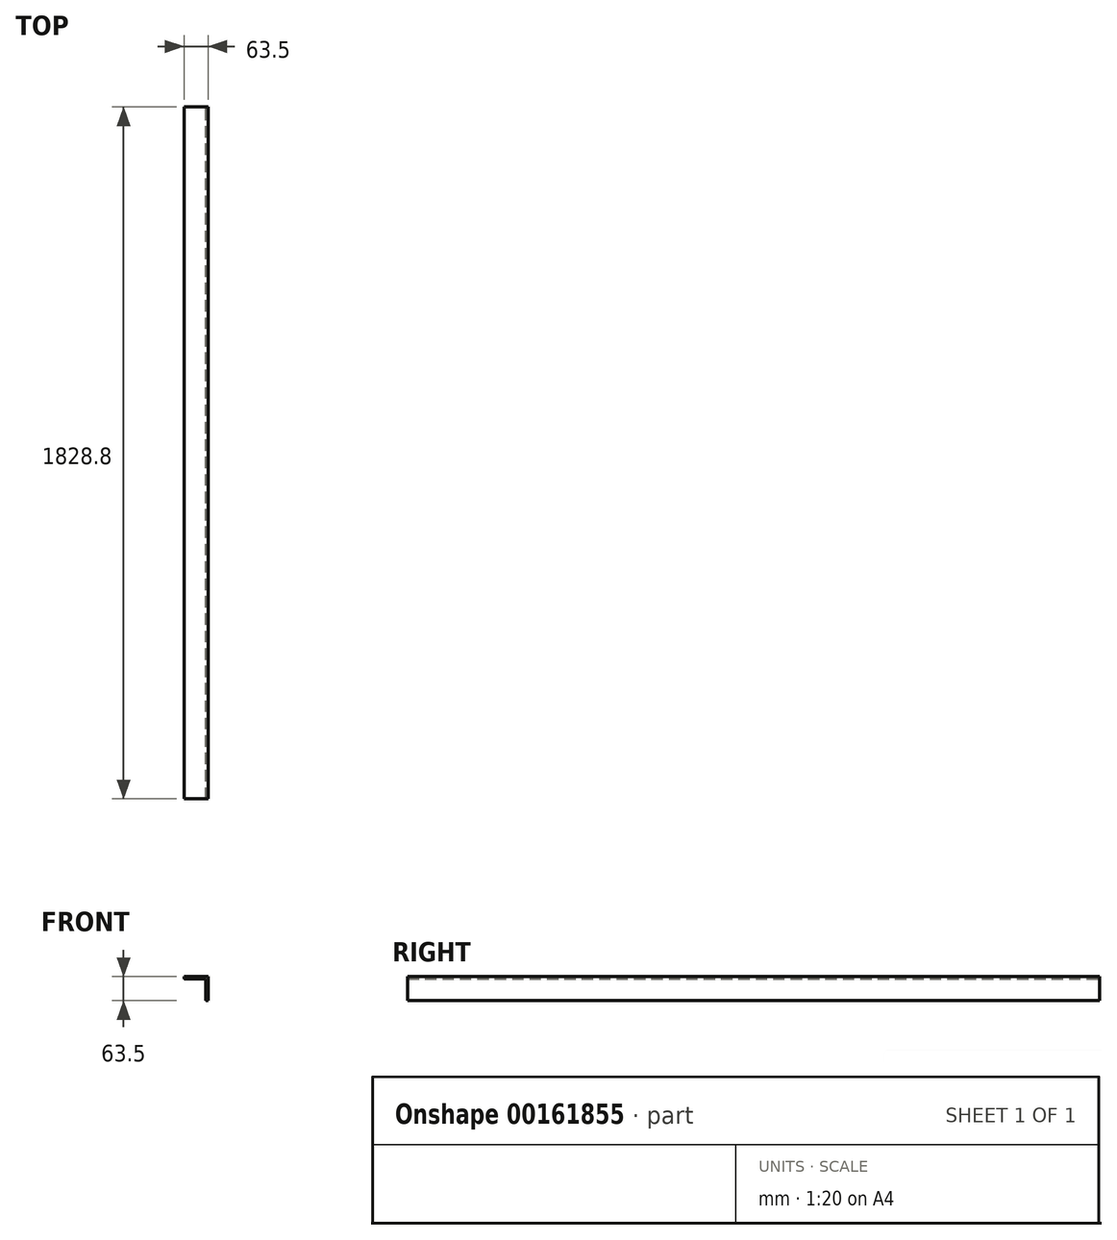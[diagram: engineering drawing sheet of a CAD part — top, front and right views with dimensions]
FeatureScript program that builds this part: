
annotation { "Feature Type Name" : "Feature", "Feature Type Description" : "" }
export const myFeature = defineFeature(function(context is Context, id is Id, definition is map)
    precondition{}
    {
        {
            var Q0;
            Q0=qCreatedBy(makeId("Front.planeOp"),FACE);
            var sketch = newSketch(context, id + "F0", { "sketchPlane" : qUnion([Q0])});
            skLineSegment(sketch, "E0", {"start": v(-82.37, 0) * mm, "end": v(-82.37, -63.5) * mm});
            skLineSegment(sketch, "E1", {"start": v(-82.37, -63.5) * mm, "end": v(-85.54, -63.5) * mm});
            skLineSegment(sketch, "E2", {"start": v(-88.72, -60.33) * mm, "end": v(-88.72, -9.52) * mm});
            skLineSegment(sketch, "E3", {"start": v(-91.9, -6.35) * mm, "end": v(-142.7, -6.35) * mm});
            skLineSegment(sketch, "E4", {"start": v(-145.87, -3.17) * mm, "end": v(-145.87, 0) * mm});
            skLineSegment(sketch, "E5", {"start": v(-145.87, 0) * mm, "end": v(-82.37, 0) * mm});
            skLineSegment(sketch, "E6", {"start": v(1187.63, 0) * mm, "end": v(1187.63, -63.5) * mm});
            skLineSegment(sketch, "E7", {"start": v(1187.63, -63.5) * mm, "end": v(1190.8, -63.5) * mm});
            skLineSegment(sketch, "E8", {"start": v(1193.98, -60.33) * mm, "end": v(1193.98, -6.35) * mm});
            skLineSegment(sketch, "E9", {"start": v(1193.98, -6.35) * mm, "end": v(1247.96, -6.35) * mm});
            skLineSegment(sketch, "E10", {"start": v(1251.13, -3.18) * mm, "end": v(1251.13, 0) * mm});
            skLineSegment(sketch, "E11", {"start": v(1251.13, 0) * mm, "end": v(1187.63, 0) * mm});
            skPoint(sketch, "E12.visualSharp", {"position": v(1193.98, -63.5) * mm});
            skArc(sketch, "E12.filletArc", {"start": v(1190.8, -63.5) * mm, "mid": v(1193.05, -62.57) * mm, "end": v(1193.98, -60.33) * mm});
            skPoint(sketch, "E13.visualSharp", {"position": v(1251.13, -6.35) * mm});
            skArc(sketch, "E13.filletArc", {"start": v(1247.96, -6.35) * mm, "mid": v(1250.2, -5.42) * mm, "end": v(1251.13, -3.18) * mm});
            skPoint(sketch, "E14.visualSharp", {"position": v(-145.87, -6.35) * mm});
            skArc(sketch, "E14.filletArc", {"start": v(-145.87, -3.17) * mm, "mid": v(-144.94, -5.42) * mm, "end": v(-142.7, -6.35) * mm});
            skPoint(sketch, "E15.visualSharp", {"position": v(-88.72, -63.5) * mm});
            skArc(sketch, "E15.filletArc", {"start": v(-88.72, -60.33) * mm, "mid": v(-87.79, -62.57) * mm, "end": v(-85.54, -63.5) * mm});
            skPoint(sketch, "E16.visualSharp", {"position": v(-88.72, -6.35) * mm});
            skArc(sketch, "E16.filletArc", {"start": v(-88.72, -9.52) * mm, "mid": v(-89.65, -7.28) * mm, "end": v(-91.9, -6.35) * mm});
            skSolve(sketch);
        }
        {
            var Q0;
            Q0=makeQuery(id+"F0.imprint","IMPRINT",FACE,{"disambiguationData":[TD([[makeQuery(id+"F0.imprint","IMPRINT",EDGE,{"derivedFrom":sQuery(id+"F0.wireOp",EDGE,"E0")}),-1.0]])]});
            extrude(context, id + "F1", {"entities" : qUnion([Q0]), "depth" : 1828.8 * mm});
        }
    });
